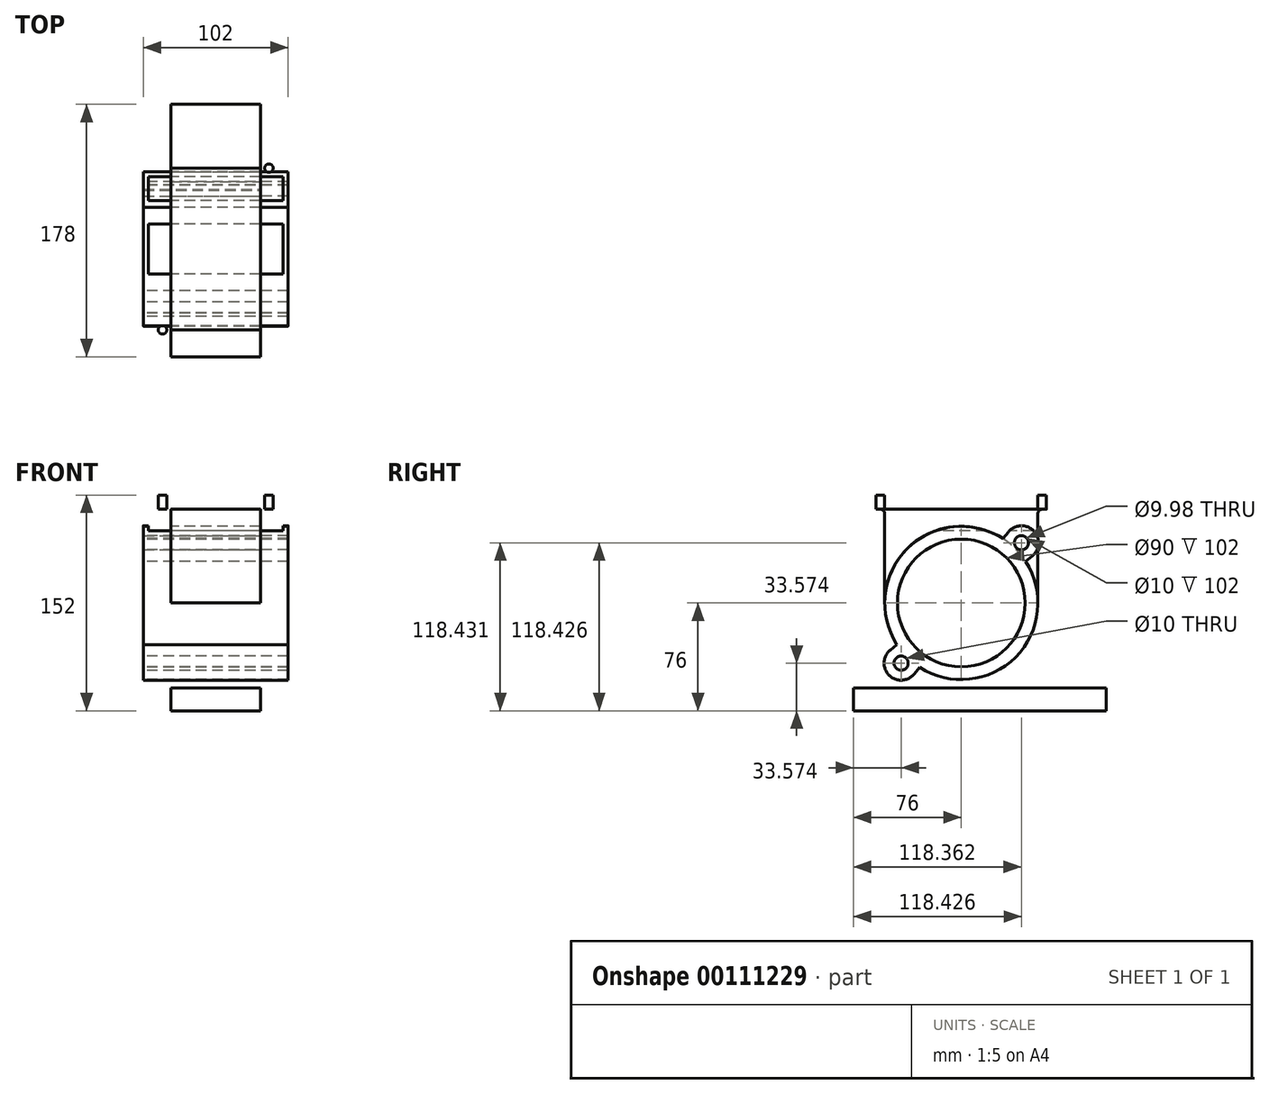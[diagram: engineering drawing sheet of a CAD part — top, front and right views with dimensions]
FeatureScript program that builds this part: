
annotation { "Feature Type Name" : "Feature", "Feature Type Description" : "" }
export const myFeature = defineFeature(function(context is Context, id is Id, definition is map)
    precondition{}
    {
        {
            var Q0;
            Q0=qCreatedBy(makeId("Right.planeOp"),FACE);
            var sketch = newSketch(context, id + "F0", { "sketchPlane" : qUnion([Q0])});
            skCircle(sketch, "E0", {"center": v(0, 0) * mm, "radius": 45 * mm});
            skArc(sketch, "E1", {"start": v(29.32, 45.35) * mm, "mid": v(-38.18, 38.18) * mm, "end": v(-45.35, -29.32) * mm});
            skCircle(sketch, "E2", {"center": v(42.43, 42.43) * mm, "radius": 5 * mm});
            skArc(sketch, "E3.trimOffspring", {"start": v(50.02, 33.14) * mm, "mid": v(50.91, 50.91) * mm, "end": v(33.14, 50.02) * mm});
            skCircle(sketch, "E4", {"center": v(-42.43, -42.43) * mm, "radius": 5 * mm});
            skArc(sketch, "E5", {"start": v(-50.02, -33.14) * mm, "mid": v(-50.91, -50.91) * mm, "end": v(-33.14, -50.02) * mm});
            skLineSegment(sketch, "E6", {"start": v(-50.02, -33.14) * mm, "end": v(-45.35, -29.32) * mm});
            skLineSegment(sketch, "E7", {"start": v(-33.14, -50.02) * mm, "end": v(-29.32, -45.35) * mm});
            skLineSegment(sketch, "E8", {"start": v(50.02, 33.14) * mm, "end": v(45.35, 29.32) * mm});
            skLineSegment(sketch, "E9", {"start": v(33.14, 50.02) * mm, "end": v(29.32, 45.35) * mm});
            skArc(sketch, "E10.trimOffspring", {"start": v(-29.32, -45.35) * mm, "mid": v(38.18, -38.18) * mm, "end": v(45.35, 29.32) * mm});
            skSolve(sketch);
        }
        {
            var Q0;
            Q0 = qSketchRegion(id + "F0", true);
            var Q1;
            Q1=makeQuery(id+"F0.imprint","IMPRINT",FACE,{"disambiguationData":[TD([[makeQuery(id+"F0.imprint","IMPRINT",EDGE,{"derivedFrom":sQuery(id+"F0.wireOp",EDGE,"E0")}),-1.0]])]});
            extrude(context, id + "F1", {"entities" : qUnion([Q0, Q1]), "endBound" : BoundingType.SYMMETRIC, "depth" : 102 * mm});
        }
        {
            var Q0;
            Q0=qCreatedBy(makeId("Top.planeOp"),FACE);
            cPlane(context, id + "F2", {"entities" : qUnion([Q0]), "cplaneType" : CPlaneType.OFFSET, "offset" : 76 * mm, "width" : 150 * mm, "height" : 150 * mm});
        }
        {
            var Q0;
            Q0=qCreatedBy(id+"F2.planeOp",FACE);
            var sketch = newSketch(context, id + "F3", { "sketchPlane" : qUnion([Q0])});
            skLineSegment(sketch, "E11.bottom", {"start": v(-47.5, 67) * mm, "end": v(47.5, 67) * mm});
            skLineSegment(sketch, "E11.top", {"start": v(-47.5, -67) * mm, "end": v(47.5, -67) * mm});
            skLineSegment(sketch, "E11.left", {"start": v(-47.5, 67) * mm, "end": v(-47.5, -67) * mm});
            skLineSegment(sketch, "E11.right", {"start": v(47.5, 67) * mm, "end": v(47.5, -67) * mm});
            skSolve(sketch);
        }
        {
            var Q0;
            Q0 = qSketchRegion(id + "F3", true);
            var Q1;
            Q1=makeQuery(id+"F3.imprint","IMPRINT",FACE,{"disambiguationData":[TD([[makeQuery(id+"F3.imprint","IMPRINT",EDGE,{"derivedFrom":sQuery(id+"F3.wireOp",EDGE,"E11.bottom")}),-1.0]])]});
            extrude(context, id + "F4", {"entities" : qUnion([Q0, Q1]), "oppositeDirection" : true, "depth" : 10 * mm});
        }
        {
            var Q0;
            Q0=makeQuery(id+"F4.opExtrude","SWEPT_EDGE",EDGE,{"disambiguationData":[OSD([sQuery(id+"F3.wireOp",EDGE,"E11.top"),sQuery(id+"F3.wireOp",EDGE,"E11.right")])]});
            var Q1;
            Q1=makeQuery(id+"F4.opExtrude","SWEPT_EDGE",EDGE,{"disambiguationData":[OSD([sQuery(id+"F3.wireOp",EDGE,"E11.bottom"),sQuery(id+"F3.wireOp",EDGE,"E11.right")])]});
            var Q2;
            Q2=makeQuery(id+"F4.opExtrude","SWEPT_EDGE",EDGE,{"disambiguationData":[OSD([sQuery(id+"F3.wireOp",EDGE,"E11.bottom"),sQuery(id+"F3.wireOp",EDGE,"E11.left")])]});
            var Q3;
            Q3=makeQuery(id+"F4.opExtrude","SWEPT_EDGE",EDGE,{"disambiguationData":[OSD([sQuery(id+"F3.wireOp",EDGE,"E11.top"),sQuery(id+"F3.wireOp",EDGE,"E11.left")])]});
            fillet(context, id + "F5", {"entities" : qUnion([Q0, Q1, Q2, Q3]), "radius" : 10 * mm, "tangentPropagation" : true, "allowEdgeOverflow" : false});
        }
        {
            var Q0;
            Q0=makeQuery(id+"F4.opExtrude","CAP_FACE",FACE,{"disambiguationData":[OSD([sQuery(id+"F3.wireOp",EDGE,"E11.bottom"),sQuery(id+"F3.wireOp",EDGE,"E11.top"),sQuery(id+"F3.wireOp",EDGE,"E11.left"),sQuery(id+"F3.wireOp",EDGE,"E11.right")])],"isStart":true});
            var sketch = newSketch(context, id + "F6", { "sketchPlane" : qUnion([Q0])});
            skCircle(sketch, "E12", {"center": v(-37.5, 57) * mm, "radius": 3 * mm});
            skCircle(sketch, "E13.MirrorC", {"center": v(37.5, 57) * mm, "radius": 3 * mm});
            skCircle(sketch, "E14.MirrorC", {"center": v(-37.5, -57) * mm, "radius": 3 * mm});
            skCircle(sketch, "E15.MirrorC", {"center": v(37.5, -57) * mm, "radius": 3 * mm});
            skSolve(sketch);
        }
        {
            var Q0;
            Q0=makeQuery(id+"F6.imprint","IMPRINT",FACE,{"disambiguationData":[TD([[makeQuery(id+"F6.imprint","IMPRINT",EDGE,{"derivedFrom":sQuery(id+"F6.wireOp",EDGE,"E15.MirrorC")}),1.0]])]});
            var Q1;
            Q1=makeQuery(id+"F6.imprint","IMPRINT",FACE,{"disambiguationData":[TD([[makeQuery(id+"F6.imprint","IMPRINT",EDGE,{"derivedFrom":sQuery(id+"F6.wireOp",EDGE,"E13.MirrorC")}),-1.0]])]});
            var Q2;
            Q2=makeQuery(id+"F6.imprint","IMPRINT",FACE,{"disambiguationData":[TD([[makeQuery(id+"F6.imprint","IMPRINT",EDGE,{"derivedFrom":sQuery(id+"F6.wireOp",EDGE,"E12")}),1.0]])]});
            var Q3;
            Q3=makeQuery(id+"F6.imprint","IMPRINT",FACE,{"disambiguationData":[TD([[makeQuery(id+"F6.imprint","IMPRINT",EDGE,{"derivedFrom":sQuery(id+"F6.wireOp",EDGE,"E14.MirrorC")}),-1.0]])]});
            extrude(context, id + "F7", {"entities" : qUnion([Q0, Q1, Q2, Q3]), "operationType" : NewBodyOperationType.REMOVE, "oppositeDirection" : true, "depth" : 25 * mm});
        }
        {
            var Q0;
            Q0=qCreatedBy(makeId("Right.planeOp"),FACE);
            var sketch = newSketch(context, id + "F8", { "sketchPlane" : qUnion([Q0])});
            skLineSegment(sketch, "E16", {"start": v(-54, 0) * mm, "end": v(-54, 63) * mm});
            skLineSegment(sketch, "E17", {"start": v(54, 0) * mm, "end": v(54, 61) * mm});
            skArc(sketch, "E18", {"start": v(54, 0) * mm, "mid": v(0, 54) * mm, "end": v(-54, 0) * mm});
            skLineSegment(sketch, "E19", {"start": v(-57, 66) * mm, "end": v(-54, 66) * mm});
            skLineSegment(sketch, "E20.MirrorCS", {"start": v(57, 66) * mm, "end": v(54, 66) * mm});
            skPoint(sketch, "E21.orphan", {"position": v(54, 66) * mm});
            skLineSegment(sketch, "E22", {"start": v(-54, 66) * mm, "end": v(54, 66) * mm});
            skArc(sketch, "E23", {"start": v(-54, 63) * mm, "mid": v(-54.88, 65.12) * mm, "end": v(-57, 66) * mm});
            skPoint(sketch, "E24.orphan", {"position": v(-54, 61) * mm});
            skPoint(sketch, "E25.orphan", {"position": v(-59.13, 66) * mm});
            skArc(sketch, "E26.MirrorCS", {"start": v(54, 63) * mm, "mid": v(54.88, 65.12) * mm, "end": v(57, 66) * mm});
            skPoint(sketch, "E27.orphan", {"position": v(59.13, 66) * mm});
            skLineSegment(sketch, "E28.MirrorCS", {"start": v(54, 0) * mm, "end": v(54, 63) * mm});
            skSolve(sketch);
        }
        {
            var Q0;
            Q0 = qSketchRegion(id + "F8", true);
            var Q1;
            Q1=makeQuery(id+"F8.imprint","IMPRINT",FACE,{"disambiguationData":[TD([[makeQuery(id+"F8.imprint","IMPRINT",EDGE,{"derivedFrom":sQuery(id+"F8.wireOp",EDGE,"E16")}),-1.0]])]});
            extrude(context, id + "F9", {"entities" : qUnion([Q0, Q1]), "endBound" : BoundingType.SYMMETRIC, "depth" : 63 * mm});
        }
        {
            var Q0;
            Q0=makeQuery(id+"F9.opExtrude","CAP_FACE",FACE,{"disambiguationData":[OSD([sQuery(id+"F8.wireOp",EDGE,"E16"),sQuery(id+"F8.wireOp",EDGE,"E17"),sQuery(id+"F8.wireOp",EDGE,"N9NgV0lg-n4zI-Go3S-eWYk-O18yg3WEL0Zh"),sQuery(id+"F8.wireOp",EDGE,"E18")])],"isStart":false});
            var sketch = newSketch(context, id + "F10", { "sketchPlane" : qUnion([Q0])});
            skCircle(sketch, "E29", {"center": v(42.36, 42.43) * mm, "radius": 5 * mm});
            skSolve(sketch);
        }
        {
            var Q0;
            Q0 = qSketchRegion(id + "F10", true);
            var Q1;
            Q1=makeQuery(id+"F10.imprint","IMPRINT",FACE,{"disambiguationData":[TD([[makeQuery(id+"F10.imprint","IMPRINT",EDGE,{"derivedFrom":sQuery(id+"F10.wireOp",EDGE,"E29")}),1.0]])]});
            extrude(context, id + "F11", {"entities" : qUnion([Q0, Q1]), "operationType" : NewBodyOperationType.REMOVE, "endBound" : BoundingType.THROUGH_ALL, "oppositeDirection" : true, "depth" : 25 * mm});
        }
        {
            var Q0;
            Q0=qCreatedBy(makeId("Top.planeOp"),FACE);
            cPlane(context, id + "F12", {"entities" : qUnion([Q0]), "cplaneType" : CPlaneType.OFFSET, "offset" : 76 * mm, "oppositeDirection" : true, "width" : 150 * mm, "height" : 150 * mm});
        }
        {
            var Q0;
            Q0=qCreatedBy(id+"F12.planeOp",FACE);
            var sketch = newSketch(context, id + "F13", { "sketchPlane" : qUnion([Q0])});
            skLineSegment(sketch, "E30.bottom", {"start": v(-31.5, -76) * mm, "end": v(31.5, -76) * mm});
            skLineSegment(sketch, "E30.top", {"start": v(-31.5, 102) * mm, "end": v(31.5, 102) * mm});
            skLineSegment(sketch, "E30.left", {"start": v(-31.5, -76) * mm, "end": v(-31.5, 102) * mm});
            skLineSegment(sketch, "E30.right", {"start": v(31.5, -76) * mm, "end": v(31.5, 102) * mm});
            skSolve(sketch);
        }
        {
            var Q0;
            Q0=makeQuery(id+"F13.imprint","IMPRINT",FACE,{"disambiguationData":[TD([[makeQuery(id+"F13.imprint","IMPRINT",EDGE,{"derivedFrom":sQuery(id+"F13.wireOp",EDGE,"E30.bottom")}),1.0]])]});
            extrude(context, id + "F14", {"entities" : qUnion([Q0]), "depth" : 16 * mm});
        }
    });
